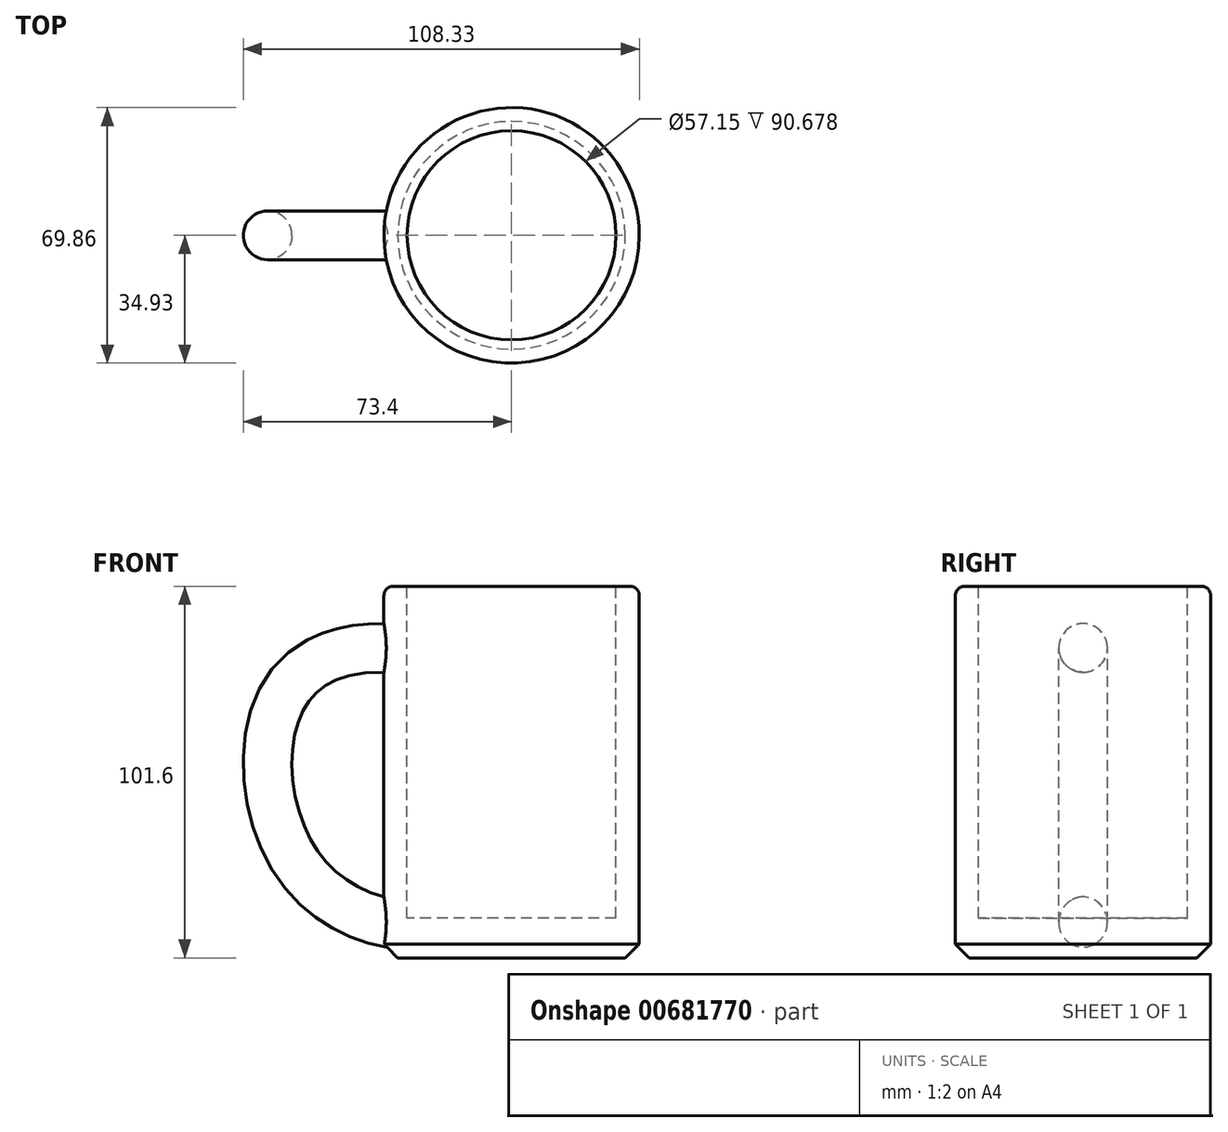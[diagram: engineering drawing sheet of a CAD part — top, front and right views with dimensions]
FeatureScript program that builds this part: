
annotation { "Feature Type Name" : "Feature", "Feature Type Description" : "" }
export const myFeature = defineFeature(function(context is Context, id is Id, definition is map)
    precondition{}
    {
        {
            var Q0;
            Q0=qCreatedBy(makeId("Top.planeOp"),FACE);
            var sketch = newSketch(context, id + "F0", { "sketchPlane" : qUnion([Q0])});
            skCircle(sketch, "E0", {"center": v(0, 0) * mm, "radius": 34.93 * mm});
            skSolve(sketch);
        }
        {
            var Q0;
            Q0=makeQuery(id+"F0.imprint","IMPRINT",FACE,{"disambiguationData":[TD([[makeQuery(id+"F0.imprint","IMPRINT",EDGE,{"derivedFrom":sQuery(id+"F0.wireOp",EDGE,"E0")}),1.0]])]});
            extrude(context, id + "F1", {"entities" : qUnion([Q0]), "depth" : 101.6 * mm, "offsetDistance" : 25.4 * mm});
        }
        {
            var Q0;
            Q0=qCreatedBy(makeId("Front.planeOp"),FACE);
            var sketch = newSketch(context, id + "F2", { "sketchPlane" : qUnion([Q0])});
            skFitSpline(sketch, "E1", {"points": [v(-33.51, 84.2) * mm, v(-64.26, 66.33) * mm, v(-58.75, 26.67) * mm, v(-27.56, 9.16) * mm], "startDerivative": vector(-159.3, 7.24) * mm, "endDerivative": vector(121.03, -10.3) * mm});
            skSolve(sketch);
        }
        {
            var Q0;
            Q0=qCreatedBy(makeId("Right.planeOp"),FACE);
            cPlane(context, id + "F3", {"entities" : qUnion([Q0]), "cplaneType" : CPlaneType.OFFSET, "offset" : 34.8 * mm, "oppositeDirection" : true, "width" : 152.4 * mm, "height" : 152.4 * mm});
        }
        {
            var Q0;
            Q0=qCreatedBy(id+"F3.planeOp",FACE);
            var sketch = newSketch(context, id + "F4", { "sketchPlane" : qUnion([Q0])});
            skCircle(sketch, "E2", {"center": v(0, 84.74) * mm, "radius": 6.65 * mm});
            skSolve(sketch);
        }
        {
            var Q0;
            Q0=makeQuery(id+"F4.imprint","IMPRINT",FACE,{"disambiguationData":[TD([[makeQuery(id+"F4.imprint","IMPRINT",EDGE,{"derivedFrom":sQuery(id+"F4.wireOp",EDGE,"E2")}),1.0]])]});
            var Q1;
            Q1=sQuery(id+"F2.wireOp",EDGE,"E1");
            sweep(context, id + "F5", {"operationType" : NewBodyOperationType.ADD, "profiles" : qUnion([Q0]), "path" : qUnion([Q1])});
        }
        {
            var Q0;
            Q0=makeQuery(id+"F1.opExtrude","CAP_FACE",FACE,{"disambiguationData":[OSD([sQuery(id+"F0.wireOp",EDGE,"E0")])],"isStart":false});
            var sketch = newSketch(context, id + "F6", { "sketchPlane" : qUnion([Q0])});
            skCircle(sketch, "E3", {"center": v(0, 0) * mm, "radius": 28.58 * mm});
            skSolve(sketch);
        }
        {
            var Q0;
            Q0=makeQuery(id+"F6.imprint","IMPRINT",FACE,{"disambiguationData":[TD([[makeQuery(id+"F6.imprint","IMPRINT",EDGE,{"derivedFrom":sQuery(id+"F6.wireOp",EDGE,"E3")}),1.0]])]});
            extrude(context, id + "F7", {"entities" : qUnion([Q0]), "operationType" : NewBodyOperationType.REMOVE, "oppositeDirection" : true, "depth" : 90.68 * mm, "offsetDistance" : 25.4 * mm});
        }
        {
            var Q0;
            Q0=makeQuery(id+"F1.opExtrude","CAP_EDGE",EDGE,{"disambiguationData":[OSD([sQuery(id+"F0.wireOp",EDGE,"E0")])],"isStart":false});
            var Q1;
            Q1=makeQuery(id+"F7.boolean.opBoolean","COPY",EDGE,{"derivedFrom":makeQuery(id+"F7.opExtrude","CAP_EDGE",EDGE,{"disambiguationData":[OSD([sQuery(id+"F6.wireOp",EDGE,"E3")])],"isStart":true})});
            fillet(context, id + "F8", {"entities" : qUnion([Q0, Q1]), "radius" : 2.54 * mm, "tangentPropagation" : true, "allowEdgeOverflow" : false});
        }
        {
            var Q0;
            Q0=makeQuery(id+"F1.opExtrude","CAP_EDGE",EDGE,{"disambiguationData":[OSD([sQuery(id+"F0.wireOp",EDGE,"E0")])],"isStart":true});
            chamfer(context, id + "F9", {"entities" : qUnion([Q0]), "width" : 3.8 * mm, "tangentPropagation" : true});
        }
    });
